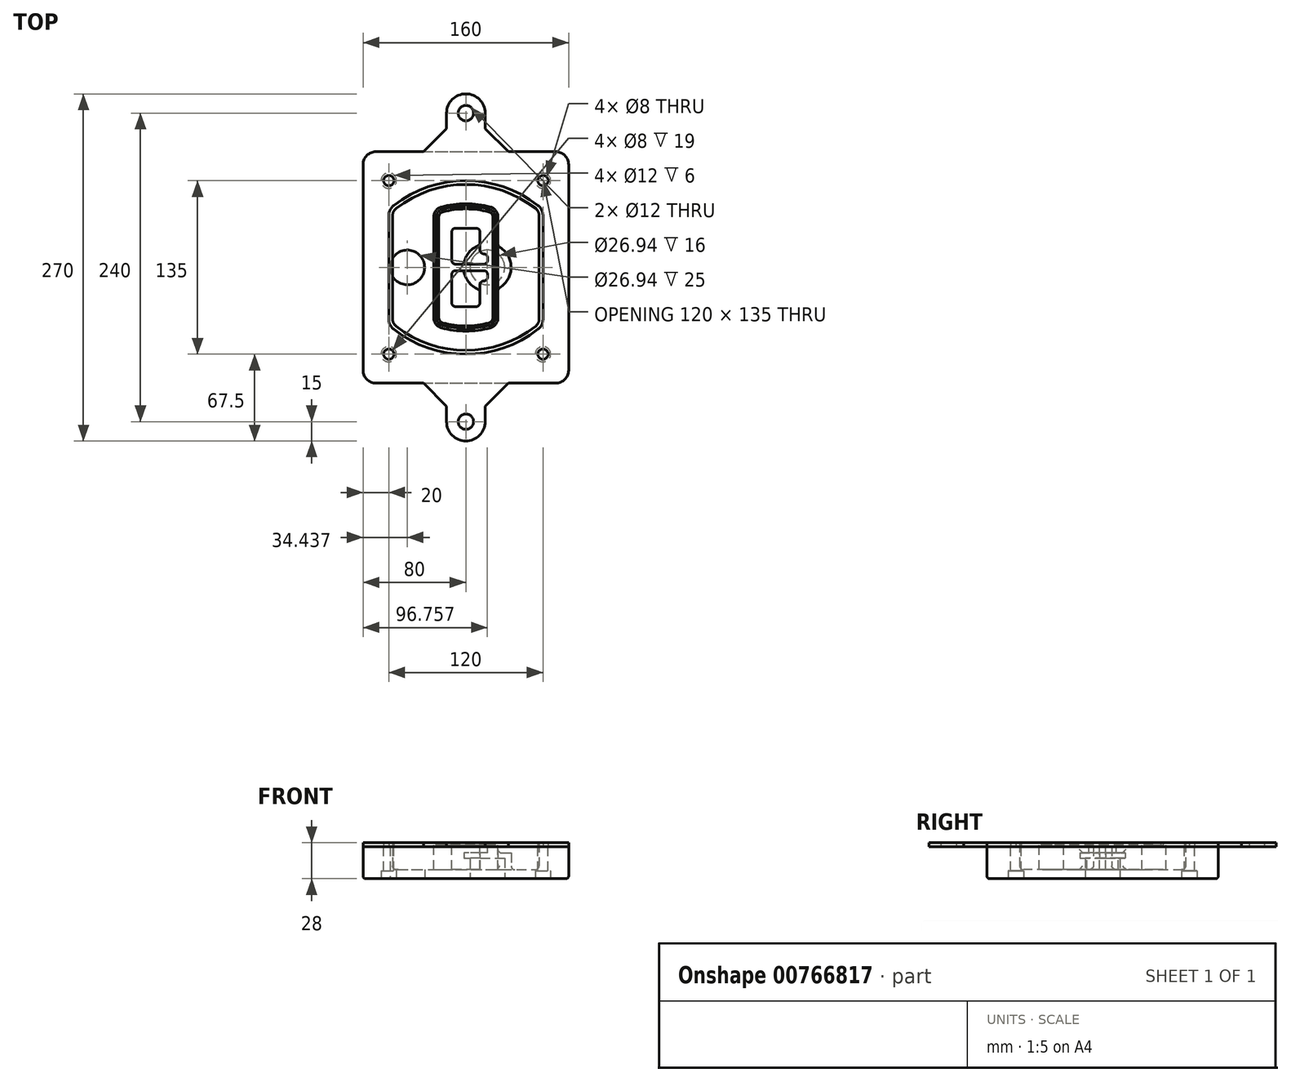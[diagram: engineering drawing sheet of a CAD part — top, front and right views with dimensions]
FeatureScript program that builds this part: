
annotation { "Feature Type Name" : "Feature", "Feature Type Description" : "" }
export const myFeature = defineFeature(function(context is Context, id is Id, definition is map)
    precondition{}
    {
        {
            var Q0;
            Q0=qCreatedBy(makeId("Top.planeOp"),FACE);
            var sketch = newSketch(context, id + "F0", { "sketchPlane" : qUnion([Q0])});
            skPoint(sketch, "E0.rect.middle", {"position": v(0, 0) * mm});
            skLineSegment(sketch, "E1.bottom", {"start": v(-70, -90) * mm, "end": v(70, -90) * mm});
            skLineSegment(sketch, "E1.top", {"start": v(-70, 90) * mm, "end": v(70, 90) * mm});
            skLineSegment(sketch, "E1.left", {"start": v(-80, -80) * mm, "end": v(-80, 80) * mm});
            skLineSegment(sketch, "E1.right", {"start": v(80, -80) * mm, "end": v(80, 80) * mm});
            skLineSegment(sketch, "E2", {"start": v(-80, 90) * mm, "end": v(80, -90) * mm, "construction": true});
            skLineSegment(sketch, "E3", {"start": v(80, 90) * mm, "end": v(-80, -90) * mm, "construction": true});
            skCircle(sketch, "E4", {"center": v(-60, 67.5) * mm, "radius": 4 * mm});
            skCircle(sketch, "E5", {"center": v(60, 67.5) * mm, "radius": 4 * mm});
            skCircle(sketch, "E6", {"center": v(60, -67.5) * mm, "radius": 4 * mm});
            skCircle(sketch, "E7", {"center": v(-60, -67.5) * mm, "radius": 4 * mm});
            skLineSegment(sketch, "E8", {"start": v(-60, 67.5) * mm, "end": v(60, 67.5) * mm, "construction": true});
            skLineSegment(sketch, "E9", {"start": v(60, 67.5) * mm, "end": v(60, -67.5) * mm, "construction": true});
            skLineSegment(sketch, "E10", {"start": v(60, -67.5) * mm, "end": v(-60, -67.5) * mm, "construction": true});
            skLineSegment(sketch, "E11", {"start": v(-60, -67.5) * mm, "end": v(-60, 67.5) * mm, "construction": true});
            skLineSegment(sketch, "E12", {"start": v(-60, 40.3) * mm, "end": v(-60, -40.3) * mm});
            skLineSegment(sketch, "E13", {"start": v(60, 40.3) * mm, "end": v(60, -40.3) * mm});
            skArc(sketch, "E14", {"start": v(56.15, 48.18) * mm, "mid": v(0, 67.5) * mm, "end": v(-56.15, 48.18) * mm});
            skArc(sketch, "E15", {"start": v(-56.15, -48.18) * mm, "mid": v(0, -67.5) * mm, "end": v(56.15, -48.18) * mm});
            skLineSegment(sketch, "E16", {"start": v(-60, 0) * mm, "end": v(60, 0) * mm, "construction": true});
            skPoint(sketch, "E17.visualSharp", {"position": v(-60, -45) * mm});
            skArc(sketch, "E17.filletArc", {"start": v(-60, -40.3) * mm, "mid": v(-58.99, -44.68) * mm, "end": v(-56.15, -48.18) * mm});
            skPoint(sketch, "E18.visualSharp", {"position": v(-60, 45) * mm});
            skArc(sketch, "E18.filletArc", {"start": v(-56.15, 48.18) * mm, "mid": v(-58.99, 44.68) * mm, "end": v(-60, 40.3) * mm});
            skPoint(sketch, "E19.visualSharp", {"position": v(60, 45) * mm});
            skArc(sketch, "E19.filletArc", {"start": v(60, 40.3) * mm, "mid": v(58.99, 44.68) * mm, "end": v(56.15, 48.18) * mm});
            skPoint(sketch, "E20.visualSharp", {"position": v(60, -45) * mm});
            skArc(sketch, "E20.filletArc", {"start": v(56.15, -48.18) * mm, "mid": v(58.99, -44.68) * mm, "end": v(60, -40.3) * mm});
            skPoint(sketch, "E21.visualSharp", {"position": v(-80, 90) * mm});
            skArc(sketch, "E21.filletArc", {"start": v(-70, 90) * mm, "mid": v(-77.07, 87.07) * mm, "end": v(-80, 80) * mm});
            skPoint(sketch, "E22.visualSharp", {"position": v(80, 90) * mm});
            skArc(sketch, "E22.filletArc", {"start": v(80, 80) * mm, "mid": v(77.07, 87.07) * mm, "end": v(70, 90) * mm});
            skPoint(sketch, "E23.visualSharp", {"position": v(80, -90) * mm});
            skArc(sketch, "E23.filletArc", {"start": v(70, -90) * mm, "mid": v(77.07, -87.07) * mm, "end": v(80, -80) * mm});
            skPoint(sketch, "E24.visualSharp", {"position": v(-80, -90) * mm});
            skArc(sketch, "E24.filletArc", {"start": v(-80, -80) * mm, "mid": v(-77.07, -87.07) * mm, "end": v(-70, -90) * mm});
            skArc(sketch, "E25.0", {"start": v(57, 40.3) * mm, "mid": v(56.3, 43.36) * mm, "end": v(54.3, 45.81) * mm});
            skLineSegment(sketch, "E25.1", {"start": v(57, 40.3) * mm, "end": v(57, -40.3) * mm});
            skArc(sketch, "E25.2", {"start": v(54.3, -45.81) * mm, "mid": v(56.3, -43.36) * mm, "end": v(57, -40.3) * mm});
            skArc(sketch, "E25.3", {"start": v(-54.3, -45.81) * mm, "mid": v(0, -64.5) * mm, "end": v(54.3, -45.81) * mm});
            skArc(sketch, "E25.4", {"start": v(-57, -40.3) * mm, "mid": v(-56.3, -43.36) * mm, "end": v(-54.3, -45.81) * mm});
            skArc(sketch, "E25.5", {"start": v(54.3, 45.81) * mm, "mid": v(0, 64.5) * mm, "end": v(-54.3, 45.81) * mm});
            skLineSegment(sketch, "E25.6", {"start": v(-57, 40.3) * mm, "end": v(-57, -40.3) * mm});
            skArc(sketch, "E25.7", {"start": v(-54.3, 45.81) * mm, "mid": v(-56.3, 43.36) * mm, "end": v(-57, 40.3) * mm});
            skArc(sketch, "E26.0", {"start": v(-58.62, 51.33) * mm, "mid": v(-62.58, 46.43) * mm, "end": v(-64, 40.3) * mm});
            skArc(sketch, "E26.1", {"start": v(58.62, 51.33) * mm, "mid": v(0, 71.5) * mm, "end": v(-58.62, 51.33) * mm});
            skArc(sketch, "E26.2", {"start": v(64, 40.3) * mm, "mid": v(62.58, 46.43) * mm, "end": v(58.62, 51.33) * mm});
            skLineSegment(sketch, "E26.3", {"start": v(64, 40.3) * mm, "end": v(64, -40.3) * mm});
            skArc(sketch, "E26.4", {"start": v(58.62, -51.33) * mm, "mid": v(62.58, -46.43) * mm, "end": v(64, -40.3) * mm});
            skLineSegment(sketch, "E26.5", {"start": v(-64, 40.3) * mm, "end": v(-64, -40.3) * mm});
            skArc(sketch, "E26.6", {"start": v(-58.62, -51.33) * mm, "mid": v(0, -71.5) * mm, "end": v(58.62, -51.33) * mm});
            skArc(sketch, "E26.7", {"start": v(-64, -40.3) * mm, "mid": v(-62.58, -46.43) * mm, "end": v(-58.62, -51.33) * mm});
            skSolve(sketch);
        }
        {
            var Q0;
            Q0=makeQuery(id+"F0.imprint","IMPRINT",FACE,{"disambiguationData":[TD([[makeQuery(id+"F0.imprint","IMPRINT",EDGE,{"derivedFrom":sQuery(id+"F0.wireOp",EDGE,"E1.bottom")}),1.0]])]});
            var Q1;
            Q1=makeQuery(id+"F0.imprint","IMPRINT",FACE,{"disambiguationData":[TD([[makeQuery(id+"F0.imprint","IMPRINT",EDGE,{"derivedFrom":sQuery(id+"F0.wireOp",EDGE,"E12")}),1.0]])]});
            var Q2;
            Q2=makeQuery(id+"F0.imprint","IMPRINT",FACE,{"disambiguationData":[TD([[makeQuery(id+"F0.imprint","IMPRINT",EDGE,{"derivedFrom":sQuery(id+"F0.wireOp",EDGE,"E25.0")}),1.0]])]});
            var Q3;
            Q3=makeQuery(id+"F0.imprint","IMPRINT",FACE,{"disambiguationData":[TD([[makeQuery(id+"F0.imprint","IMPRINT",EDGE,{"derivedFrom":sQuery(id+"F0.wireOp",EDGE,"E12")}),-1.0]])]});
            extrude(context, id + "F1", {"entities" : qUnion([Q0, Q1, Q2, Q3]), "oppositeDirection" : true, "depth" : 25 * mm});
        }
        {
            var Q0;
            Q0=makeQuery(id+"F0.imprint","IMPRINT",FACE,{"disambiguationData":[TD([[makeQuery(id+"F0.imprint","IMPRINT",EDGE,{"derivedFrom":sQuery(id+"F0.wireOp",EDGE,"E12")}),1.0]])]});
            extrude(context, id + "F2", {"entities" : qUnion([Q0]), "operationType" : NewBodyOperationType.ADD, "depth" : 3 * mm});
        }
        {
            var Q0;
            Q0=makeQuery(id+"F0.imprint","IMPRINT",FACE,{"disambiguationData":[TD([[makeQuery(id+"F0.imprint","IMPRINT",EDGE,{"derivedFrom":sQuery(id+"F0.wireOp",EDGE,"E25.0")}),1.0]])]});
            extrude(context, id + "F3", {"entities" : qUnion([Q0]), "operationType" : NewBodyOperationType.REMOVE, "oppositeDirection" : true, "depth" : 18 * mm});
        }
        {
            var Q0;
            Q0=makeQuery(id+"F2.opExtrude","CAP_FACE",FACE,{"disambiguationData":[OSD([sQuery(id+"F0.wireOp",EDGE,"E12"),sQuery(id+"F0.wireOp",EDGE,"E13"),sQuery(id+"F0.wireOp",EDGE,"E14"),sQuery(id+"F0.wireOp",EDGE,"E15"),sQuery(id+"F0.wireOp",EDGE,"E17.filletArc"),sQuery(id+"F0.wireOp",EDGE,"E18.filletArc"),sQuery(id+"F0.wireOp",EDGE,"E19.filletArc"),sQuery(id+"F0.wireOp",EDGE,"E20.filletArc"),sQuery(id+"F0.wireOp",EDGE,"E25.0"),sQuery(id+"F0.wireOp",EDGE,"E25.1"),sQuery(id+"F0.wireOp",EDGE,"E25.2"),sQuery(id+"F0.wireOp",EDGE,"E25.3"),sQuery(id+"F0.wireOp",EDGE,"E25.4"),sQuery(id+"F0.wireOp",EDGE,"E25.5"),sQuery(id+"F0.wireOp",EDGE,"E25.6"),sQuery(id+"F0.wireOp",EDGE,"E25.7")])],"isStart":false});
            var sketch = newSketch(context, id + "F4", { "sketchPlane" : qUnion([Q0])});
            skArc(sketch, "E27.0", {"start": v(-19.08, -46.97) * mm, "mid": v(0, -49.5) * mm, "end": v(19.08, -46.97) * mm});
            skArc(sketch, "E28.0", {"start": v(19.08, 46.97) * mm, "mid": v(0, 49.5) * mm, "end": v(-19.08, 46.97) * mm});
            skLineSegment(sketch, "E29", {"start": v(-25, 39.25) * mm, "end": v(-25, -39.25) * mm});
            skLineSegment(sketch, "E30", {"start": v(25, 39.25) * mm, "end": v(25, -39.25) * mm});
            skLineSegment(sketch, "E31", {"start": v(-25, 45.1) * mm, "end": v(25, 45.1) * mm, "construction": true});
            skLineSegment(sketch, "E32", {"start": v(-25, -45.1) * mm, "end": v(25, -45.1) * mm, "construction": true});
            skPoint(sketch, "E33.visualSharp", {"position": v(-25, 45.1) * mm});
            skArc(sketch, "E33.filletArc", {"start": v(-19.08, 46.97) * mm, "mid": v(-23.35, 44.11) * mm, "end": v(-25, 39.25) * mm});
            skPoint(sketch, "E34.visualSharp", {"position": v(25, 45.1) * mm});
            skArc(sketch, "E34.filletArc", {"start": v(25, 39.25) * mm, "mid": v(23.35, 44.11) * mm, "end": v(19.08, 46.97) * mm});
            skPoint(sketch, "E35.visualSharp", {"position": v(25, -45.1) * mm});
            skArc(sketch, "E35.filletArc", {"start": v(19.08, -46.97) * mm, "mid": v(23.35, -44.11) * mm, "end": v(25, -39.25) * mm});
            skPoint(sketch, "E36.visualSharp", {"position": v(-25, -45.1) * mm});
            skArc(sketch, "E36.filletArc", {"start": v(-25, -39.25) * mm, "mid": v(-23.35, -44.11) * mm, "end": v(-19.08, -46.97) * mm});
            skArc(sketch, "E37.0", {"start": v(54.3, 45.81) * mm, "mid": v(0, 64.5) * mm, "end": v(-54.3, 45.81) * mm});
            skArc(sketch, "E37.1", {"start": v(-54.3, 45.81) * mm, "mid": v(-56.3, 43.36) * mm, "end": v(-57, 40.3) * mm});
            skLineSegment(sketch, "E37.2", {"start": v(-57, 40.3) * mm, "end": v(-57, -40.3) * mm});
            skArc(sketch, "E37.3", {"start": v(-57, -40.3) * mm, "mid": v(-56.3, -43.36) * mm, "end": v(-54.3, -45.81) * mm});
            skArc(sketch, "E37.4", {"start": v(-54.3, -45.81) * mm, "mid": v(0, -64.5) * mm, "end": v(54.3, -45.81) * mm});
            skArc(sketch, "E37.5", {"start": v(54.3, -45.81) * mm, "mid": v(56.3, -43.36) * mm, "end": v(57, -40.3) * mm});
            skLineSegment(sketch, "E37.6", {"start": v(57, 40.3) * mm, "end": v(57, -40.3) * mm});
            skArc(sketch, "E37.7", {"start": v(57, 40.3) * mm, "mid": v(56.3, 43.36) * mm, "end": v(54.3, 45.81) * mm});
            skLineSegment(sketch, "E38.0", {"start": v(23, 39.25) * mm, "end": v(23, -39.25) * mm});
            skArc(sketch, "E38.1", {"start": v(18.56, -45.04) * mm, "mid": v(21.76, -42.9) * mm, "end": v(23, -39.25) * mm});
            skArc(sketch, "E38.2", {"start": v(-18.56, -45.04) * mm, "mid": v(0, -47.5) * mm, "end": v(18.56, -45.04) * mm});
            skArc(sketch, "E38.3", {"start": v(-23, -39.25) * mm, "mid": v(-21.76, -42.9) * mm, "end": v(-18.56, -45.04) * mm});
            skLineSegment(sketch, "E38.4", {"start": v(-23, 39.25) * mm, "end": v(-23, -39.25) * mm});
            skArc(sketch, "E38.5", {"start": v(23, 39.25) * mm, "mid": v(21.76, 42.9) * mm, "end": v(18.56, 45.04) * mm});
            skArc(sketch, "E38.6", {"start": v(-18.56, 45.04) * mm, "mid": v(-21.76, 42.9) * mm, "end": v(-23, 39.25) * mm});
            skArc(sketch, "E38.7", {"start": v(18.56, 45.04) * mm, "mid": v(0, 47.5) * mm, "end": v(-18.56, 45.04) * mm});
            skArc(sketch, "E39.0", {"start": v(21, 39.25) * mm, "mid": v(20.18, 41.68) * mm, "end": v(18.04, 43.1) * mm});
            skLineSegment(sketch, "E39.1", {"start": v(21, 39.25) * mm, "end": v(21, -39.25) * mm});
            skArc(sketch, "E39.2", {"start": v(18.04, -43.1) * mm, "mid": v(20.18, -41.68) * mm, "end": v(21, -39.25) * mm});
            skArc(sketch, "E39.3", {"start": v(-18.04, -43.1) * mm, "mid": v(0, -45.5) * mm, "end": v(18.04, -43.1) * mm});
            skArc(sketch, "E39.4", {"start": v(-21, -39.25) * mm, "mid": v(-20.18, -41.68) * mm, "end": v(-18.04, -43.1) * mm});
            skArc(sketch, "E39.5", {"start": v(18.04, 43.1) * mm, "mid": v(0, 45.5) * mm, "end": v(-18.04, 43.1) * mm});
            skLineSegment(sketch, "E39.6", {"start": v(-21, 39.25) * mm, "end": v(-21, -39.25) * mm});
            skArc(sketch, "E39.7", {"start": v(-18.04, 43.1) * mm, "mid": v(-20.18, 41.68) * mm, "end": v(-21, 39.25) * mm});
            skLineSegment(sketch, "E40", {"start": v(-25, 0) * mm, "end": v(25, 0) * mm, "construction": true});
            skLineSegment(sketch, "E41", {"start": v(-11, 5.5) * mm, "end": v(-11, 27.5) * mm});
            skLineSegment(sketch, "E42", {"start": v(-8, 30.5) * mm, "end": v(8, 30.5) * mm});
            skLineSegment(sketch, "E43", {"start": v(11, 27.5) * mm, "end": v(11, 13.5) * mm});
            skLineSegment(sketch, "E44", {"start": v(14, 10.5) * mm, "end": v(14, 10.5) * mm});
            skLineSegment(sketch, "E45", {"start": v(17, 7.5) * mm, "end": v(17, 5.5) * mm});
            skLineSegment(sketch, "E46", {"start": v(14, 2.5) * mm, "end": v(-8, 2.5) * mm});
            skPoint(sketch, "E47.visualSharp", {"position": v(-11, 30.5) * mm});
            skArc(sketch, "E47.filletArc", {"start": v(-8, 30.5) * mm, "mid": v(-10.12, 29.62) * mm, "end": v(-11, 27.5) * mm});
            skPoint(sketch, "E48.visualSharp", {"position": v(11, 30.5) * mm});
            skArc(sketch, "E48.filletArc", {"start": v(11, 27.5) * mm, "mid": v(10.12, 29.62) * mm, "end": v(8, 30.5) * mm});
            skPoint(sketch, "E49.visualSharp", {"position": v(11, 10.5) * mm});
            skArc(sketch, "E49.filletArc", {"start": v(11, 13.5) * mm, "mid": v(11.88, 11.38) * mm, "end": v(14, 10.5) * mm});
            skPoint(sketch, "E50.visualSharp", {"position": v(17, 10.5) * mm});
            skArc(sketch, "E50.filletArc", {"start": v(17, 7.5) * mm, "mid": v(16.12, 9.62) * mm, "end": v(14, 10.5) * mm});
            skPoint(sketch, "E51.visualSharp", {"position": v(17, 2.5) * mm});
            skArc(sketch, "E51.filletArc", {"start": v(14, 2.5) * mm, "mid": v(16.12, 3.38) * mm, "end": v(17, 5.5) * mm});
            skPoint(sketch, "E52.visualSharp", {"position": v(-11, 2.5) * mm});
            skArc(sketch, "E52.filletArc", {"start": v(-11, 5.5) * mm, "mid": v(-10.12, 3.38) * mm, "end": v(-8, 2.5) * mm});
            skLineSegment(sketch, "E53.0.MirrorCS", {"start": v(14, -2.5) * mm, "end": v(-8, -2.5) * mm});
            skArc(sketch, "E54.0.MirrorCS", {"start": v(-11, -5.5) * mm, "mid": v(-10.12, -3.38) * mm, "end": v(-8, -2.5) * mm});
            skLineSegment(sketch, "E55.0.MirrorCS", {"start": v(-11, -5.5) * mm, "end": v(-11, -27.5) * mm});
            skArc(sketch, "E56.0.MirrorCS", {"start": v(-8, -30.5) * mm, "mid": v(-10.12, -29.62) * mm, "end": v(-11, -27.5) * mm});
            skLineSegment(sketch, "E57.0.MirrorCS", {"start": v(-8, -30.5) * mm, "end": v(8, -30.5) * mm});
            skArc(sketch, "E58.0.MirrorCS", {"start": v(11, -27.5) * mm, "mid": v(10.12, -29.62) * mm, "end": v(8, -30.5) * mm});
            skLineSegment(sketch, "E59.0.MirrorCS", {"start": v(11, -27.5) * mm, "end": v(11, -13.5) * mm});
            skArc(sketch, "E60.0.MirrorCS", {"start": v(11, -13.5) * mm, "mid": v(11.88, -11.38) * mm, "end": v(14, -10.5) * mm});
            skArc(sketch, "E61.0.MirrorCS", {"start": v(17, -7.5) * mm, "mid": v(16.12, -9.62) * mm, "end": v(14, -10.5) * mm});
            skLineSegment(sketch, "E62.0.MirrorCS", {"start": v(17, -7.5) * mm, "end": v(17, -5.5) * mm});
            skArc(sketch, "E63.0.MirrorCS", {"start": v(14, -2.5) * mm, "mid": v(16.12, -3.38) * mm, "end": v(17, -5.5) * mm});
            skSolve(sketch);
        }
        {
            var Q0;
            Q0=makeQuery(id+"F4.imprint","IMPRINT",FACE,{"disambiguationData":[TD([[makeQuery(id+"F4.imprint","IMPRINT",EDGE,{"derivedFrom":sQuery(id+"F4.wireOp",EDGE,"E27.0")}),1.0]])]});
            var Q1;
            Q1=makeQuery(id+"F4.imprint","IMPRINT",FACE,{"disambiguationData":[TD([[makeQuery(id+"F4.imprint","IMPRINT",EDGE,{"derivedFrom":sQuery(id+"F4.wireOp",EDGE,"E38.0")}),-1.0]])]});
            var Q2;
            Q2=makeQuery(id+"F4.imprint","IMPRINT",FACE,{"disambiguationData":[TD([[makeQuery(id+"F4.imprint","IMPRINT",EDGE,{"derivedFrom":sQuery(id+"F4.wireOp",EDGE,"E39.0")}),1.0]])]});
            extrude(context, id + "F5", {"entities" : qUnion([Q0, Q1, Q2]), "operationType" : NewBodyOperationType.ADD, "endBound" : BoundingType.UP_TO_NEXT, "oppositeDirection" : true, "depth" : 25 * mm});
        }
        {
            var Q0;
            Q0=makeQuery(id+"F4.imprint","IMPRINT",FACE,{"disambiguationData":[TD([[makeQuery(id+"F4.imprint","IMPRINT",EDGE,{"derivedFrom":sQuery(id+"F4.wireOp",EDGE,"E38.0")}),-1.0]])]});
            extrude(context, id + "F6", {"entities" : qUnion([Q0]), "operationType" : NewBodyOperationType.REMOVE, "oppositeDirection" : true, "depth" : 2 * mm});
        }
        {
            var Q0;
            Q0=makeQuery(id+"F1.opExtrude","CAP_FACE",FACE,{"disambiguationData":[OSD([sQuery(id+"F0.wireOp",EDGE,"E1.bottom"),sQuery(id+"F0.wireOp",EDGE,"E1.top"),sQuery(id+"F0.wireOp",EDGE,"E1.left"),sQuery(id+"F0.wireOp",EDGE,"E1.right"),sQuery(id+"F0.wireOp",EDGE,"E4"),sQuery(id+"F0.wireOp",EDGE,"E5"),sQuery(id+"F0.wireOp",EDGE,"E6"),sQuery(id+"F0.wireOp",EDGE,"E7"),sQuery(id+"F0.wireOp",EDGE,"E21.filletArc"),sQuery(id+"F0.wireOp",EDGE,"E22.filletArc"),sQuery(id+"F0.wireOp",EDGE,"E23.filletArc"),sQuery(id+"F0.wireOp",EDGE,"E24.filletArc")])],"isStart":false});
            var sketch = newSketch(context, id + "F7", { "sketchPlane" : qUnion([Q0])});
            skCircle(sketch, "E64", {"center": v(16.76, 0) * mm, "radius": 13.47 * mm});
            skCircle(sketch, "E65", {"center": v(-45.56, 0) * mm, "radius": 13.47 * mm});
            skLineSegment(sketch, "E66", {"start": v(80, 0) * mm, "end": v(-80, 0) * mm});
            skCircle(sketch, "E67", {"center": v(16.76, 0) * mm, "radius": 18.47 * mm});
            skCircle(sketch, "E68", {"center": v(60, -67.5) * mm, "radius": 6 * mm});
            skCircle(sketch, "E69", {"center": v(-60, -67.5) * mm, "radius": 6 * mm});
            skCircle(sketch, "E70", {"center": v(-60, 67.5) * mm, "radius": 6 * mm});
            skCircle(sketch, "E71", {"center": v(60, 67.5) * mm, "radius": 6 * mm});
            skSolve(sketch);
        }
        {
            var Q0;
            {var subQ1=sQuery(id+"F7.wireOp",EDGE,"E66");var subQ4=sQuery(id+"F7.wireOp",EDGE,"E64");var subQ6=makeQuery(id+"F7.imprint","INTERSECT",VERTEX,{"disambiguationData":[OD(0.0)],"derivedFrom":[subQ4,subQ1]});Q0=makeQuery(id+"F7.imprint","IMPRINT",FACE,{"disambiguationData":[TD([[makeQuery(id+"F7.imprint","IMPRINT",EDGE,{"disambiguationData":[TD([[subQ6,-1.0]])],"derivedFrom":subQ4}),-1.0]])]});}
            var Q1;
            {var subQ0=sQuery(id+"F7.wireOp",EDGE,"E66");var subQ1=sQuery(id+"F7.wireOp",EDGE,"E64");var subQ3=makeQuery(id+"F7.imprint","INTERSECT",VERTEX,{"disambiguationData":[OD(0.0)],"derivedFrom":[subQ1,subQ0]});Q1=makeQuery(id+"F7.imprint","IMPRINT",FACE,{"disambiguationData":[TD([[makeQuery(id+"F7.imprint","IMPRINT",EDGE,{"disambiguationData":[TD([[subQ3,-1.0]])],"derivedFrom":subQ1}),1.0]])]});}
            var Q2;
            {var subQ0=sQuery(id+"F7.wireOp",EDGE,"E66");var subQ1=sQuery(id+"F7.wireOp",EDGE,"E64");var subQ3=makeQuery(id+"F7.imprint","INTERSECT",VERTEX,{"disambiguationData":[OD(0.0)],"derivedFrom":[subQ1,subQ0]});Q2=makeQuery(id+"F7.imprint","IMPRINT",FACE,{"disambiguationData":[TD([[makeQuery(id+"F7.imprint","IMPRINT",EDGE,{"disambiguationData":[TD([[subQ3,1.0]])],"derivedFrom":subQ1}),1.0]])]});}
            var Q3;
            {var subQ1=sQuery(id+"F7.wireOp",EDGE,"E66");var subQ4=sQuery(id+"F7.wireOp",EDGE,"E64");var subQ6=makeQuery(id+"F7.imprint","INTERSECT",VERTEX,{"disambiguationData":[OD(0.0)],"derivedFrom":[subQ4,subQ1]});Q3=makeQuery(id+"F7.imprint","IMPRINT",FACE,{"disambiguationData":[TD([[makeQuery(id+"F7.imprint","IMPRINT",EDGE,{"disambiguationData":[TD([[subQ6,1.0]])],"derivedFrom":subQ4}),-1.0]])]});}
            extrude(context, id + "F8", {"entities" : qUnion([Q0, Q1, Q2, Q3]), "operationType" : NewBodyOperationType.ADD, "oppositeDirection" : true, "depth" : 20 * mm});
        }
        {
            var Q0;
            {var subQ0=sQuery(id+"F7.wireOp",EDGE,"E66");var subQ1=sQuery(id+"F7.wireOp",EDGE,"E64");var subQ3=makeQuery(id+"F7.imprint","INTERSECT",VERTEX,{"disambiguationData":[OD(0.0)],"derivedFrom":[subQ1,subQ0]});Q0=makeQuery(id+"F7.imprint","IMPRINT",FACE,{"disambiguationData":[TD([[makeQuery(id+"F7.imprint","IMPRINT",EDGE,{"disambiguationData":[TD([[subQ3,-1.0]])],"derivedFrom":subQ1}),1.0]])]});}
            var Q1;
            {var subQ0=sQuery(id+"F7.wireOp",EDGE,"E66");var subQ1=sQuery(id+"F7.wireOp",EDGE,"E64");var subQ3=makeQuery(id+"F7.imprint","INTERSECT",VERTEX,{"disambiguationData":[OD(0.0)],"derivedFrom":[subQ1,subQ0]});Q1=makeQuery(id+"F7.imprint","IMPRINT",FACE,{"disambiguationData":[TD([[makeQuery(id+"F7.imprint","IMPRINT",EDGE,{"disambiguationData":[TD([[subQ3,1.0]])],"derivedFrom":subQ1}),1.0]])]});}
            extrude(context, id + "F9", {"entities" : qUnion([Q0, Q1]), "operationType" : NewBodyOperationType.REMOVE, "oppositeDirection" : true, "depth" : 16 * mm});
        }
        {
            var Q0;
            {var subQ0=sQuery(id+"F7.wireOp",EDGE,"E66");var subQ1=sQuery(id+"F7.wireOp",EDGE,"E65");var subQ3=makeQuery(id+"F7.imprint","INTERSECT",VERTEX,{"disambiguationData":[OD(0.0)],"derivedFrom":[subQ1,subQ0]});Q0=makeQuery(id+"F7.imprint","IMPRINT",FACE,{"disambiguationData":[TD([[makeQuery(id+"F7.imprint","IMPRINT",EDGE,{"disambiguationData":[TD([[subQ3,-1.0]])],"derivedFrom":subQ1}),1.0]])]});}
            var Q1;
            {var subQ0=sQuery(id+"F7.wireOp",EDGE,"E66");var subQ1=sQuery(id+"F7.wireOp",EDGE,"E65");var subQ3=makeQuery(id+"F7.imprint","INTERSECT",VERTEX,{"disambiguationData":[OD(0.0)],"derivedFrom":[subQ1,subQ0]});Q1=makeQuery(id+"F7.imprint","IMPRINT",FACE,{"disambiguationData":[TD([[makeQuery(id+"F7.imprint","IMPRINT",EDGE,{"disambiguationData":[TD([[subQ3,1.0]])],"derivedFrom":subQ1}),1.0]])]});}
            extrude(context, id + "F10", {"entities" : qUnion([Q0, Q1]), "operationType" : NewBodyOperationType.REMOVE, "oppositeDirection" : true, "depth" : 25 * mm});
        }
        {
            var Q0;
            Q0=makeQuery(id+"F7.imprint","IMPRINT",FACE,{"disambiguationData":[TD([[makeQuery(id+"F7.imprint","IMPRINT",EDGE,{"derivedFrom":sQuery(id+"F7.wireOp",EDGE,"E68")}),1.0]])]});
            var Q1;
            Q1=makeQuery(id+"F7.imprint","IMPRINT",FACE,{"disambiguationData":[TD([[makeQuery(id+"F7.imprint","IMPRINT",EDGE,{"derivedFrom":makeQuery(id+"F1.opExtrude","CAP_EDGE",EDGE,{"disambiguationData":[OSD([sQuery(id+"F0.wireOp",EDGE,"E5")])],"isStart":false})}),-1.0]])]});
            var Q2;
            Q2=makeQuery(id+"F7.imprint","IMPRINT",FACE,{"disambiguationData":[TD([[makeQuery(id+"F7.imprint","IMPRINT",EDGE,{"derivedFrom":sQuery(id+"F7.wireOp",EDGE,"E69")}),1.0]])]});
            var Q3;
            Q3=makeQuery(id+"F7.imprint","IMPRINT",FACE,{"disambiguationData":[TD([[makeQuery(id+"F7.imprint","IMPRINT",EDGE,{"derivedFrom":makeQuery(id+"F1.opExtrude","CAP_EDGE",EDGE,{"disambiguationData":[OSD([sQuery(id+"F0.wireOp",EDGE,"E4")])],"isStart":false})}),-1.0]])]});
            var Q4;
            Q4=makeQuery(id+"F7.imprint","IMPRINT",FACE,{"disambiguationData":[TD([[makeQuery(id+"F7.imprint","IMPRINT",EDGE,{"derivedFrom":sQuery(id+"F7.wireOp",EDGE,"E70")}),1.0]])]});
            var Q5;
            Q5=makeQuery(id+"F7.imprint","IMPRINT",FACE,{"disambiguationData":[TD([[makeQuery(id+"F7.imprint","IMPRINT",EDGE,{"derivedFrom":makeQuery(id+"F1.opExtrude","CAP_EDGE",EDGE,{"disambiguationData":[OSD([sQuery(id+"F0.wireOp",EDGE,"E7")])],"isStart":false})}),-1.0]])]});
            var Q6;
            Q6=makeQuery(id+"F7.imprint","IMPRINT",FACE,{"disambiguationData":[TD([[makeQuery(id+"F7.imprint","IMPRINT",EDGE,{"derivedFrom":sQuery(id+"F7.wireOp",EDGE,"E71")}),1.0]])]});
            var Q7;
            Q7=makeQuery(id+"F7.imprint","IMPRINT",FACE,{"disambiguationData":[TD([[makeQuery(id+"F7.imprint","IMPRINT",EDGE,{"derivedFrom":makeQuery(id+"F1.opExtrude","CAP_EDGE",EDGE,{"disambiguationData":[OSD([sQuery(id+"F0.wireOp",EDGE,"E6")])],"isStart":false})}),-1.0]])]});
            extrude(context, id + "F11", {"entities" : qUnion([Q0, Q1, Q2, Q3, Q4, Q5, Q6, Q7]), "operationType" : NewBodyOperationType.REMOVE, "oppositeDirection" : true, "depth" : 6 * mm});
        }
        {
            var Q0;
            Q0=makeQuery(id+"F9.boolean.opBoolean","COPY",FACE,{"derivedFrom":makeQuery(id+"F9.opExtrude","CAP_FACE",FACE,{"disambiguationData":[OSD([sQuery(id+"F7.wireOp",EDGE,"E64")])],"isStart":false})});
            var sketch = newSketch(context, id + "F12", { "sketchPlane" : qUnion([Q0])});
            skArc(sketch, "E72.0", {"start": v(11, 17.55) * mm, "mid": v(2.57, 11.82) * mm, "end": v(-1.54, 2.5) * mm});
            skArc(sketch, "E72.1", {"start": v(-1.54, -2.5) * mm, "mid": v(2.57, -11.82) * mm, "end": v(11, -17.55) * mm});
            skLineSegment(sketch, "E73", {"start": v(-1.54, -2.5) * mm, "end": v(14, -2.5) * mm});
            skLineSegment(sketch, "E74.0", {"start": v(14, 2.5) * mm, "end": v(-1.54, 2.5) * mm});
            skArc(sketch, "E74.1", {"start": v(14, 2.5) * mm, "mid": v(16.12, 3.38) * mm, "end": v(17, 5.5) * mm});
            skLineSegment(sketch, "E74.2", {"start": v(17, 7.5) * mm, "end": v(17, 5.5) * mm});
            skArc(sketch, "E74.3", {"start": v(17, 7.5) * mm, "mid": v(16.12, 9.62) * mm, "end": v(14, 10.5) * mm});
            skArc(sketch, "E74.4", {"start": v(11, 13.5) * mm, "mid": v(11.88, 11.38) * mm, "end": v(14, 10.5) * mm});
            skLineSegment(sketch, "E74.5", {"start": v(11, 17.55) * mm, "end": v(11, 13.5) * mm});
            skLineSegment(sketch, "E74.7", {"start": v(14, -2.5) * mm, "end": v(-1.54, -2.5) * mm});
            skArc(sketch, "E74.8", {"start": v(14, -2.5) * mm, "mid": v(16.12, -3.38) * mm, "end": v(17, -5.5) * mm});
            skLineSegment(sketch, "E74.9", {"start": v(17, -7.5) * mm, "end": v(17, -5.5) * mm});
            skArc(sketch, "E74.10", {"start": v(17, -7.5) * mm, "mid": v(16.12, -9.62) * mm, "end": v(14, -10.5) * mm});
            skArc(sketch, "E74.11", {"start": v(11, -13.5) * mm, "mid": v(11.88, -11.38) * mm, "end": v(14, -10.5) * mm});
            skLineSegment(sketch, "E74.12", {"start": v(11, -17.55) * mm, "end": v(11, -13.5) * mm});
            skPoint(sketch, "E75.orphan", {"position": v(11, -27.5) * mm});
            skPoint(sketch, "E76.orphan", {"position": v(-8, -2.5) * mm});
            skPoint(sketch, "E77.orphan", {"position": v(-8, 2.5) * mm});
            skPoint(sketch, "E78.orphan", {"position": v(11, 27.5) * mm});
            skSolve(sketch);
        }
        {
            var Q0;
            {var subQ7=sQuery(id+"F12.wireOp",EDGE,"E72.0");var subQ14=sQuery(id+"F12.wireOp",EDGE,"E72.1");var subQ16=sQuery(id+"F12.wireOp",EDGE,"E74.1");var subQ18=sQuery(id+"F12.wireOp",EDGE,"E74.8");Q0=qUnion([makeQuery(id+"F12.imprint","IMPRINT",FACE,{"disambiguationData":[TD([[makeQuery(id+"F12.imprint","IMPRINT",EDGE,{"derivedFrom":subQ7}),1.0]])]}),makeQuery(id+"F12.imprint","IMPRINT",FACE,{"disambiguationData":[TD([[makeQuery(id+"F12.imprint","IMPRINT",EDGE,{"derivedFrom":subQ14}),1.0]])]}),makeQuery(id+"F12.imprint","IMPRINT",FACE,{"disambiguationData":[TD([[makeQuery(id+"F12.imprint","IMPRINT",EDGE,{"derivedFrom":subQ16}),1.0]])]}),makeQuery(id+"F12.imprint","IMPRINT",FACE,{"disambiguationData":[TD([[makeQuery(id+"F12.imprint","IMPRINT",EDGE,{"derivedFrom":subQ18}),-1.0]])]})]);}
            var Q1;
            Q1=makeQuery(id+"F5.boolean.opBoolean","SPLIT",FACE,{"disambiguationData":[TD([makeQuery(id+"F5.opExtrude","SWEPT_FACE",FACE,{"disambiguationData":[OSD([sQuery(id+"F4.wireOp",EDGE,"E41")])]})])],"derivedFrom":makeQuery(id+"F3.boolean.opBoolean","COPY",FACE,{"derivedFrom":makeQuery(id+"F3.opExtrude","CAP_FACE",FACE,{"disambiguationData":[OSD([sQuery(id+"F0.wireOp",EDGE,"E25.0"),sQuery(id+"F0.wireOp",EDGE,"E25.1"),sQuery(id+"F0.wireOp",EDGE,"E25.2"),sQuery(id+"F0.wireOp",EDGE,"E25.3"),sQuery(id+"F0.wireOp",EDGE,"E25.4"),sQuery(id+"F0.wireOp",EDGE,"E25.5"),sQuery(id+"F0.wireOp",EDGE,"E25.6"),sQuery(id+"F0.wireOp",EDGE,"E25.7")])],"isStart":false})})});
            extrude(context, id + "F13", {"entities" : qUnion([Q0]), "operationType" : NewBodyOperationType.REMOVE, "endBound" : BoundingType.UP_TO_SURFACE, "endBoundEntityFace" : qUnion([Q1]), "depth" : 25 * mm});
        }
        {
            var Q0;
            Q0=makeQuery(id+"F3.boolean.opBoolean","COPY",EDGE,{"derivedFrom":makeQuery(id+"F3.opExtrude","CAP_EDGE",EDGE,{"disambiguationData":[OSD([sQuery(id+"F0.wireOp",EDGE,"E25.6")])],"isStart":false})});
            var Q1;
            Q1=makeQuery(id+"F8.boolean.opBoolean","INTERSECT",EDGE,{"derivedFrom":[makeQuery(id+"F5.opExtrude","SWEPT_FACE",FACE,{"disambiguationData":[OSD([sQuery(id+"F4.wireOp",EDGE,"E30")])]}),makeQuery(id+"F8.opExtrude","CAP_FACE",FACE,{"disambiguationData":[OSD([sQuery(id+"F7.wireOp",EDGE,"E67")])],"isStart":false})]});
            var Q2;
            Q2=makeQuery(id+"F8.boolean.opBoolean","INTERSECT",EDGE,{"disambiguationData":[OD(1.0)],"derivedFrom":[makeQuery(id+"F5.opExtrude","SWEPT_FACE",FACE,{"disambiguationData":[OSD([sQuery(id+"F4.wireOp",EDGE,"E30")])]}),makeQuery(id+"F8.opExtrude","SWEPT_FACE",FACE,{"disambiguationData":[OSD([sQuery(id+"F7.wireOp",EDGE,"E67")])]})]});
            var Q3;
            {var subQ0=sQuery(id+"F4.wireOp",EDGE,"E30");Q3=makeQuery(id+"F8.boolean.opBoolean","SPLIT",EDGE,{"disambiguationData":[TD([makeQuery(id+"F5.opExtrude","SWEPT_FACE",FACE,{"disambiguationData":[OSD([sQuery(id+"F4.wireOp",EDGE,"E35.filletArc")])]})])],"derivedFrom":makeQuery(id+"F5.opExtrude","CAP_EDGE",EDGE,{"disambiguationData":[OSD([subQ0])],"isStart":false})});}
            var Q4;
            {var subQ0=sQuery(id+"F0.wireOp",EDGE,"E25.7");var subQ1=sQuery(id+"F0.wireOp",EDGE,"E25.1");var subQ2=sQuery(id+"F0.wireOp",EDGE,"E25.6");var subQ3=sQuery(id+"F0.wireOp",EDGE,"E25.5");var subQ4=sQuery(id+"F0.wireOp",EDGE,"E25.4");var subQ5=sQuery(id+"F0.wireOp",EDGE,"E25.0");var subQ6=sQuery(id+"F0.wireOp",EDGE,"E25.2");var subQ7=sQuery(id+"F0.wireOp",EDGE,"E25.3");Q4=makeQuery(id+"F8.boolean.opBoolean","INTERSECT",EDGE,{"derivedFrom":[makeQuery(id+"F5.boolean.opBoolean","SPLIT",FACE,{"disambiguationData":[TD([makeQuery(id+"F2.opExtrude","SWEPT_FACE",FACE,{"disambiguationData":[OSD([subQ5])]})])],"derivedFrom":makeQuery(id+"F3.boolean.opBoolean","COPY",FACE,{"derivedFrom":makeQuery(id+"F3.opExtrude","CAP_FACE",FACE,{"disambiguationData":[OSD([subQ5,subQ1,subQ6,subQ7,subQ4,subQ3,subQ2,subQ0])],"isStart":false})})}),makeQuery(id+"F8.opExtrude","SWEPT_FACE",FACE,{"disambiguationData":[OSD([sQuery(id+"F7.wireOp",EDGE,"E67")])]})]});}
            var Q5;
            Q5=makeQuery(id+"F8.boolean.opBoolean","INTERSECT",EDGE,{"disambiguationData":[OD(0.0)],"derivedFrom":[makeQuery(id+"F5.opExtrude","SWEPT_FACE",FACE,{"disambiguationData":[OSD([sQuery(id+"F4.wireOp",EDGE,"E30")])]}),makeQuery(id+"F8.opExtrude","SWEPT_FACE",FACE,{"disambiguationData":[OSD([sQuery(id+"F7.wireOp",EDGE,"E67")])]})]});
            fillet(context, id + "F14", {"entities" : qUnion([Q0, Q1, Q2, Q3, Q4, Q5]), "radius" : 3 * mm, "tangentPropagation" : true, "allowEdgeOverflow" : false});
        }
        {
            var Q0;
            Q0=makeQuery(id+"F1.opExtrude","CAP_EDGE",EDGE,{"disambiguationData":[OSD([sQuery(id+"F0.wireOp",EDGE,"E1.bottom")])],"isStart":false});
            fillet(context, id + "F15", {"entities" : qUnion([Q0]), "radius" : 2 * mm, "tangentPropagation" : true, "allowEdgeOverflow" : false});
        }
        {
            var Q0;
            {var subQ0=sQuery(id+"F0.wireOp",EDGE,"E21.filletArc");var subQ1=sQuery(id+"F0.wireOp",EDGE,"E7");var subQ2=sQuery(id+"F0.wireOp",EDGE,"E6");var subQ3=sQuery(id+"F0.wireOp",EDGE,"E5");var subQ4=sQuery(id+"F0.wireOp",EDGE,"E4");var subQ5=sQuery(id+"F0.wireOp",EDGE,"E22.filletArc");var subQ6=sQuery(id+"F0.wireOp",EDGE,"E1.bottom");var subQ7=sQuery(id+"F0.wireOp",EDGE,"E1.right");var subQ8=sQuery(id+"F0.wireOp",EDGE,"E1.top");var subQ9=sQuery(id+"F0.wireOp",EDGE,"E1.left");var subQ10=sQuery(id+"F0.wireOp",EDGE,"E23.filletArc");var subQ11=sQuery(id+"F0.wireOp",EDGE,"E24.filletArc");Q0=makeQuery(id+"F2.boolean.opBoolean","SPLIT",FACE,{"disambiguationData":[TD([makeQuery(id+"F1.opExtrude","SWEPT_FACE",FACE,{"disambiguationData":[OSD([subQ6])]})])],"derivedFrom":makeQuery(id+"F1.opExtrude","CAP_FACE",FACE,{"disambiguationData":[OSD([subQ6,subQ8,subQ9,subQ7,subQ4,subQ3,subQ2,subQ1,subQ0,subQ5,subQ10,subQ11])],"isStart":true})});}
            var sketch = newSketch(context, id + "F16", { "sketchPlane" : qUnion([Q0])});
            skLineSegment(sketch, "E79", {"start": v(0, 90) * mm, "end": v(0, 120) * mm, "construction": true});
            skCircle(sketch, "E80", {"center": v(0, 120) * mm, "radius": 6 * mm});
            skArc(sketch, "E81", {"start": v(15, 120) * mm, "mid": v(0, 135) * mm, "end": v(-15, 120) * mm});
            skLineSegment(sketch, "E82", {"start": v(15, 120) * mm, "end": v(15, 108) * mm});
            skLineSegment(sketch, "E83", {"start": v(-15, 108) * mm, "end": v(-15, 120) * mm});
            skLineSegment(sketch, "E84", {"start": v(-15, 108) * mm, "end": v(-33, 90) * mm});
            skLineSegment(sketch, "E85", {"start": v(15, 108) * mm, "end": v(33, 90) * mm});
            skLineSegment(sketch, "E86", {"start": v(-80, 0) * mm, "end": v(80, 0) * mm, "construction": true});
            skLineSegment(sketch, "E87.MirrorCS", {"start": v(-15, -108) * mm, "end": v(-33, -90) * mm});
            skLineSegment(sketch, "E88.MirrorCS", {"start": v(-15, -108) * mm, "end": v(-15, -120) * mm});
            skArc(sketch, "E89.MirrorCS", {"start": v(15, -120) * mm, "mid": v(0, -135) * mm, "end": v(-15, -120) * mm});
            skLineSegment(sketch, "E90.MirrorCS", {"start": v(15, -120) * mm, "end": v(15, -108) * mm});
            skLineSegment(sketch, "E91.MirrorCS", {"start": v(15, -108) * mm, "end": v(33, -90) * mm});
            skCircle(sketch, "E92.MirrorC", {"center": v(0, -120) * mm, "radius": 6 * mm});
            skLineSegment(sketch, "E93.MirrorCS", {"start": v(0, -90) * mm, "end": v(0, -120) * mm, "construction": true});
            skSolve(sketch);
        }
        {
            var Q0;
            Q0=makeQuery(id+"F16.imprint","IMPRINT",FACE,{"disambiguationData":[TD([[makeQuery(id+"F16.imprint","IMPRINT",EDGE,{"derivedFrom":sQuery(id+"F16.wireOp",EDGE,"E80")}),-1.0]])]});
            var Q1;
            {var subQ0=sQuery(id+"F16.wireOp",EDGE,"E87.MirrorCS");Q1=makeQuery(id+"F16.imprint","IMPRINT",FACE,{"disambiguationData":[TD([[makeQuery(id+"F16.imprint","IMPRINT",EDGE,{"derivedFrom":subQ0}),-1.0]])]});}
            var Q2;
            Q2=makeQuery(id+"F16.imprint","IMPRINT",FACE,{"disambiguationData":[TD([[makeQuery(id+"F16.imprint","IMPRINT",EDGE,{"derivedFrom":makeQuery(id+"F1.opExtrude","CAP_EDGE",EDGE,{"disambiguationData":[OSD([sQuery(id+"F0.wireOp",EDGE,"E1.left")])],"isStart":true})}),-1.0]])]});
            var Q3;
            Q3=makeQuery(id+"F2.opExtrude","CAP_FACE",FACE,{"disambiguationData":[OSD([sQuery(id+"F0.wireOp",EDGE,"E12"),sQuery(id+"F0.wireOp",EDGE,"E13"),sQuery(id+"F0.wireOp",EDGE,"E14"),sQuery(id+"F0.wireOp",EDGE,"E15"),sQuery(id+"F0.wireOp",EDGE,"E17.filletArc"),sQuery(id+"F0.wireOp",EDGE,"E18.filletArc"),sQuery(id+"F0.wireOp",EDGE,"E19.filletArc"),sQuery(id+"F0.wireOp",EDGE,"E20.filletArc"),sQuery(id+"F0.wireOp",EDGE,"E25.0"),sQuery(id+"F0.wireOp",EDGE,"E25.1"),sQuery(id+"F0.wireOp",EDGE,"E25.2"),sQuery(id+"F0.wireOp",EDGE,"E25.3"),sQuery(id+"F0.wireOp",EDGE,"E25.4"),sQuery(id+"F0.wireOp",EDGE,"E25.5"),sQuery(id+"F0.wireOp",EDGE,"E25.6"),sQuery(id+"F0.wireOp",EDGE,"E25.7")])],"isStart":false});
            extrude(context, id + "F17", {"entities" : qUnion([Q0, Q1, Q2]), "endBound" : BoundingType.UP_TO_SURFACE, "depth" : 25 * mm, "endBoundEntityFace" : qUnion([Q3]), "offsetDistance" : 25 * mm});
        }
    });
